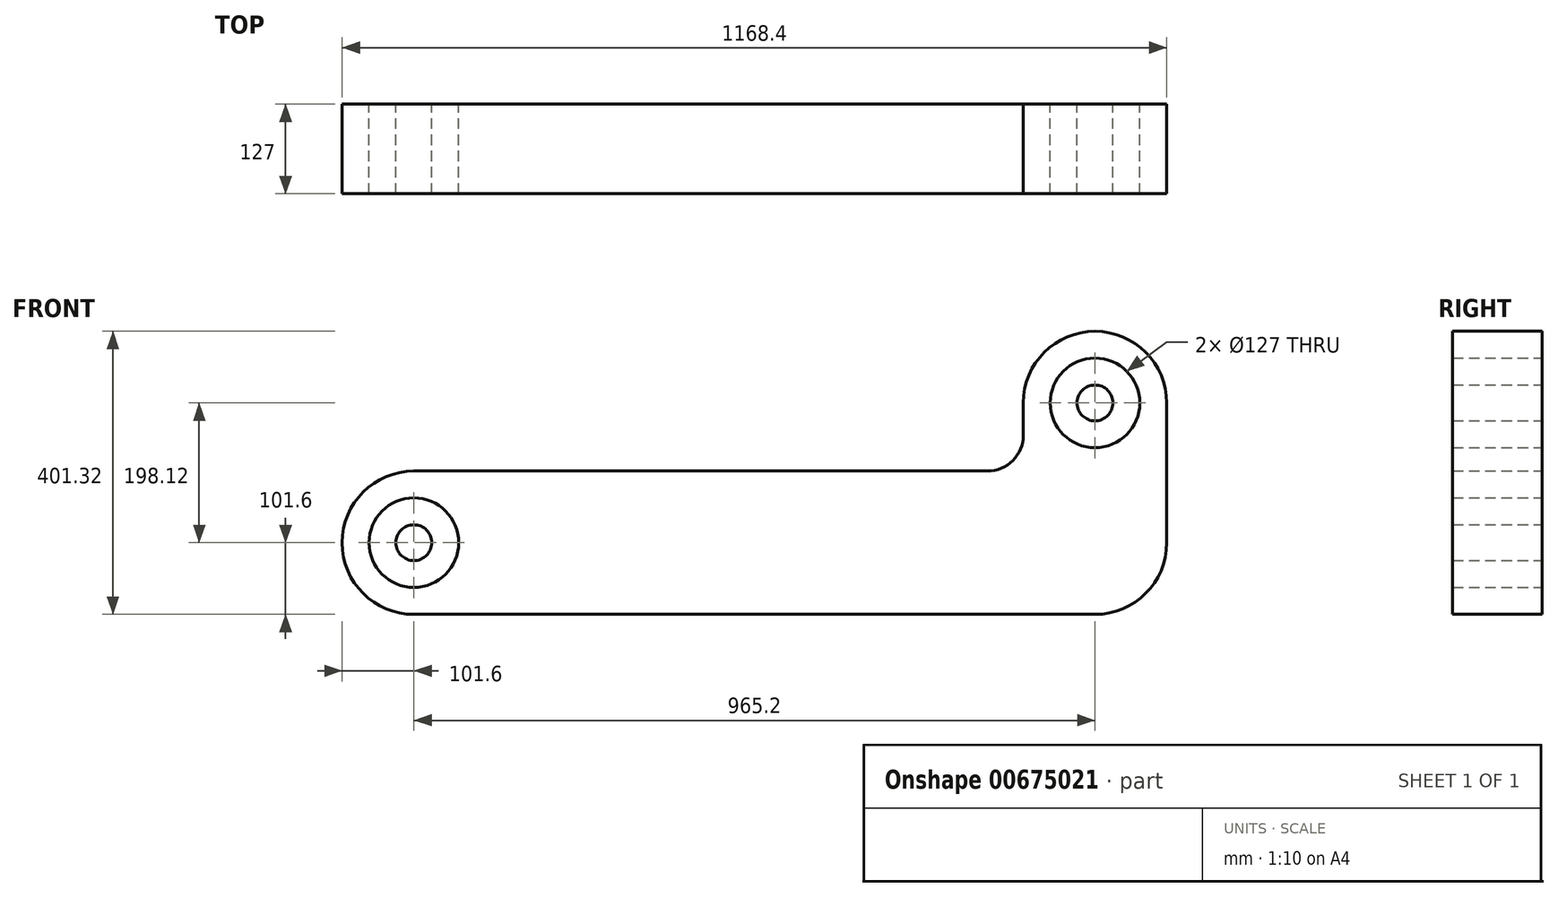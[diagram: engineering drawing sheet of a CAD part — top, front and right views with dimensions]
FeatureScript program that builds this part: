
annotation { "Feature Type Name" : "Feature", "Feature Type Description" : "" }
export const myFeature = defineFeature(function(context is Context, id is Id, definition is map)
    precondition{}
    {
        {
            var Q0;
            Q0=qCreatedBy(makeId("Front.planeOp"),FACE);
            var sketch = newSketch(context, id + "F0", { "sketchPlane" : qUnion([Q0])});
            skLineSegment(sketch, "E0.bottom", {"start": v(0, 0) * mm, "end": v(965.2, 0) * mm});
            skLineSegment(sketch, "E0.top", {"start": v(0, 203.2) * mm, "end": v(812.8, 203.2) * mm});
            skArc(sketch, "E1", {"start": v(0, 203.2) * mm, "mid": v(-101.6, 101.6) * mm, "end": v(0, 0) * mm});
            skArc(sketch, "E2", {"start": v(965.2, 0) * mm, "mid": v(1037.04, 29.76) * mm, "end": v(1066.8, 101.6) * mm});
            skLineSegment(sketch, "E3.bottom", {"start": v(863.6, 0) * mm, "end": v(965.2, 0) * mm});
            skLineSegment(sketch, "E3.left", {"start": v(863.6, 254) * mm, "end": v(863.6, 299.72) * mm});
            skLineSegment(sketch, "E3.right", {"start": v(1066.8, 101.6) * mm, "end": v(1066.8, 299.72) * mm});
            skArc(sketch, "E4", {"start": v(1066.8, 299.72) * mm, "mid": v(965.2, 401.32) * mm, "end": v(863.6, 299.72) * mm});
            skCircle(sketch, "E5", {"center": v(0, 101.6) * mm, "radius": 63.5 * mm});
            skCircle(sketch, "E6", {"center": v(0, 101.6) * mm, "radius": 25.4 * mm});
            skCircle(sketch, "E7", {"center": v(965.2, 299.72) * mm, "radius": 63.5 * mm});
            skCircle(sketch, "E8", {"center": v(965.2, 299.72) * mm, "radius": 25.4 * mm});
            skPoint(sketch, "E9.visualSharp", {"position": v(863.6, 203.2) * mm});
            skArc(sketch, "E9.filletArc", {"start": v(812.8, 203.2) * mm, "mid": v(848.72, 218.08) * mm, "end": v(863.6, 254) * mm});
            skSolve(sketch);
        }
        {
            var Q0;
            Q0=makeQuery(id+"F0.imprint","IMPRINT",FACE,{"disambiguationData":[TD([[makeQuery(id+"F0.imprint","IMPRINT",EDGE,{"derivedFrom":sQuery(id+"F0.wireOp",EDGE,"E0.bottom")}),1.0]])]});
            var Q1;
            Q1=makeQuery(id+"F0.imprint","IMPRINT",FACE,{"disambiguationData":[TD([[makeQuery(id+"F0.imprint","IMPRINT",EDGE,{"derivedFrom":sQuery(id+"F0.wireOp",EDGE,"E6")}),1.0]])]});
            var Q2;
            Q2=makeQuery(id+"F0.imprint","IMPRINT",FACE,{"disambiguationData":[TD([[makeQuery(id+"F0.imprint","IMPRINT",EDGE,{"derivedFrom":sQuery(id+"F0.wireOp",EDGE,"E8")}),1.0]])]});
            extrude(context, id + "F1", {"entities" : qUnion([Q0, Q1, Q2]), "depth" : 127 * mm, "offsetDistance" : 25.4 * mm});
        }
    });
